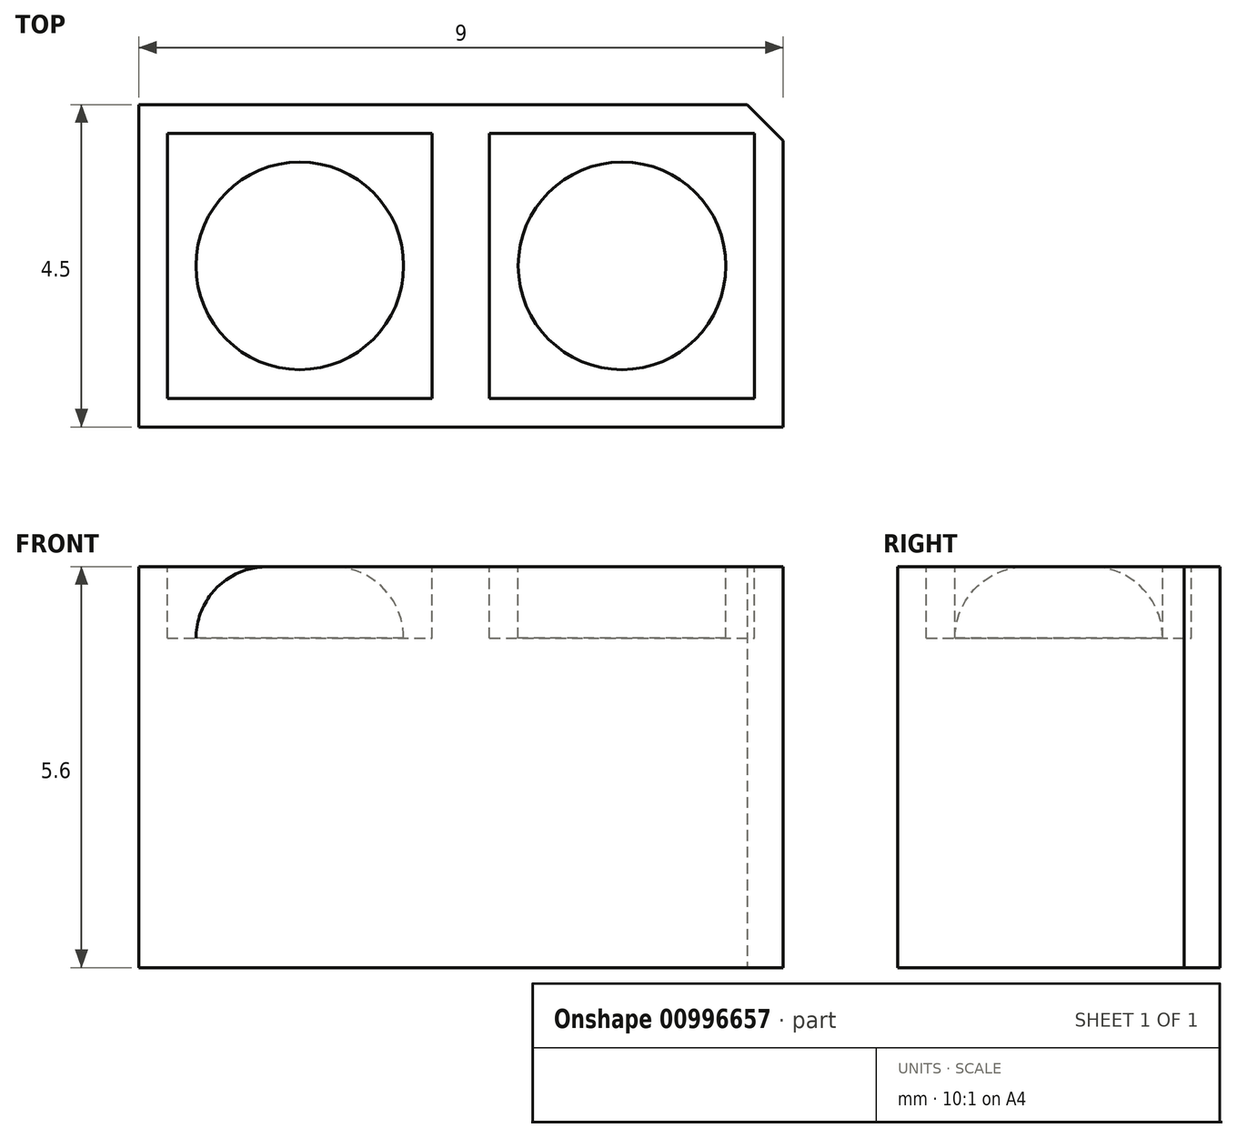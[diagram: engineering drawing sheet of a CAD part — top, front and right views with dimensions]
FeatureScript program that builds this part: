
annotation { "Feature Type Name" : "Feature", "Feature Type Description" : "" }
export const myFeature = defineFeature(function(context is Context, id is Id, definition is map)
    precondition{}
    {
        {
            var Q0;
            Q0=qCreatedBy(makeId("Top.planeOp"),FACE);
            var sketch = newSketch(context, id + "F0", { "sketchPlane" : qUnion([Q0])});
            skLineSegment(sketch, "E0.bottom", {"start": v(4.5, 2.25) * mm, "end": v(-4.5, 2.25) * mm});
            skLineSegment(sketch, "E0.top", {"start": v(4.5, -2.25) * mm, "end": v(-4.5, -2.25) * mm});
            skLineSegment(sketch, "E0.left", {"start": v(4.5, 2.25) * mm, "end": v(4.5, -2.25) * mm});
            skLineSegment(sketch, "E0.right", {"start": v(-4.5, 2.25) * mm, "end": v(-4.5, -2.25) * mm});
            skPoint(sketch, "E0.middle", {"position": v(0, 0) * mm});
            skSolve(sketch);
        }
        {
            var Q0;
            Q0 = qSketchRegion(id + "F0", true);
            extrude(context, id + "F1", {"entities" : qUnion([Q0]), "depth" : 5.6 * mm, "offsetDistance" : 25 * mm});
        }
        {
            var Q0;
            Q0=makeQuery(id+"F1.opExtrude","CAP_FACE",FACE,{"disambiguationData":[OSD([sQuery(id+"F0.wireOp",EDGE,"E0.bottom"),sQuery(id+"F0.wireOp",EDGE,"E0.top"),sQuery(id+"F0.wireOp",EDGE,"E0.left"),sQuery(id+"F0.wireOp",EDGE,"E0.right")])],"isStart":false});
            var sketch = newSketch(context, id + "F2", { "sketchPlane" : qUnion([Q0])});
            skLineSegment(sketch, "E1", {"start": v(0, 2.25) * mm, "end": v(0, -2.25) * mm, "construction": true});
            skLineSegment(sketch, "E2", {"start": v(0, 0) * mm, "end": v(-4.5, 0) * mm, "construction": true});
            skLineSegment(sketch, "E3", {"start": v(0, 0) * mm, "end": v(4.5, 0) * mm, "construction": true});
            skCircle(sketch, "E4", {"center": v(-2.25, 0) * mm, "radius": 1.45 * mm});
            skCircle(sketch, "E5", {"center": v(2.25, 0) * mm, "radius": 1.45 * mm});
            skLineSegment(sketch, "E6.bottom", {"start": v(-4.1, -1.85) * mm, "end": v(-0.4, -1.85) * mm});
            skLineSegment(sketch, "E6.top", {"start": v(-4.1, 1.85) * mm, "end": v(-0.4, 1.85) * mm});
            skLineSegment(sketch, "E6.left", {"start": v(-4.1, -1.85) * mm, "end": v(-4.1, 1.85) * mm});
            skLineSegment(sketch, "E6.right", {"start": v(-0.4, -1.85) * mm, "end": v(-0.4, 1.85) * mm});
            skLineSegment(sketch, "E7.bottom", {"start": v(0.4, -1.85) * mm, "end": v(4.1, -1.85) * mm});
            skLineSegment(sketch, "E7.top", {"start": v(0.4, 1.85) * mm, "end": v(4.1, 1.85) * mm});
            skLineSegment(sketch, "E7.left", {"start": v(0.4, -1.85) * mm, "end": v(0.4, 1.85) * mm});
            skLineSegment(sketch, "E7.right", {"start": v(4.1, -1.85) * mm, "end": v(4.1, 1.85) * mm});
            skSolve(sketch);
        }
        {
            var Q0;
            Q0 = qSketchRegion(id + "F2", true);
            extrude(context, id + "F3", {"entities" : qUnion([Q0]), "operationType" : NewBodyOperationType.REMOVE, "oppositeDirection" : true, "depth" : 1 * mm, "offsetDistance" : 25 * mm});
        }
        {
            var Q0;
            Q0=makeQuery(id+"F3.boolean.opBoolean","COPY",EDGE,{"derivedFrom":makeQuery(id+"F3.opExtrude","CAP_EDGE",EDGE,{"disambiguationData":[OSD([sQuery(id+"F2.wireOp",EDGE,"E4")])],"isStart":true})});
            var Q1;
            Q1=makeQuery(id+"F3.boolean.opBoolean","COPY",EDGE,{"derivedFrom":makeQuery(id+"F3.opExtrude","CAP_EDGE",EDGE,{"disambiguationData":[OSD([sQuery(id+"F2.wireOp",EDGE,"E5")])],"isStart":true})});
            fillet(context, id + "F4", {"entities" : qUnion([Q0, Q1]), "radius" : 1 * mm, "tangentPropagation" : true, "allowEdgeOverflow" : false});
        }
        {
            var Q0;
            Q0=makeQuery(id+"F1.opExtrude","SWEPT_EDGE",EDGE,{"disambiguationData":[OSD([sQuery(id+"F0.wireOp",EDGE,"E0.bottom"),sQuery(id+"F0.wireOp",EDGE,"E0.left")])]});
            chamfer(context, id + "F5", {"entities" : qUnion([Q0]), "width" : 0.5 * mm, "tangentPropagation" : true});
        }
    });
